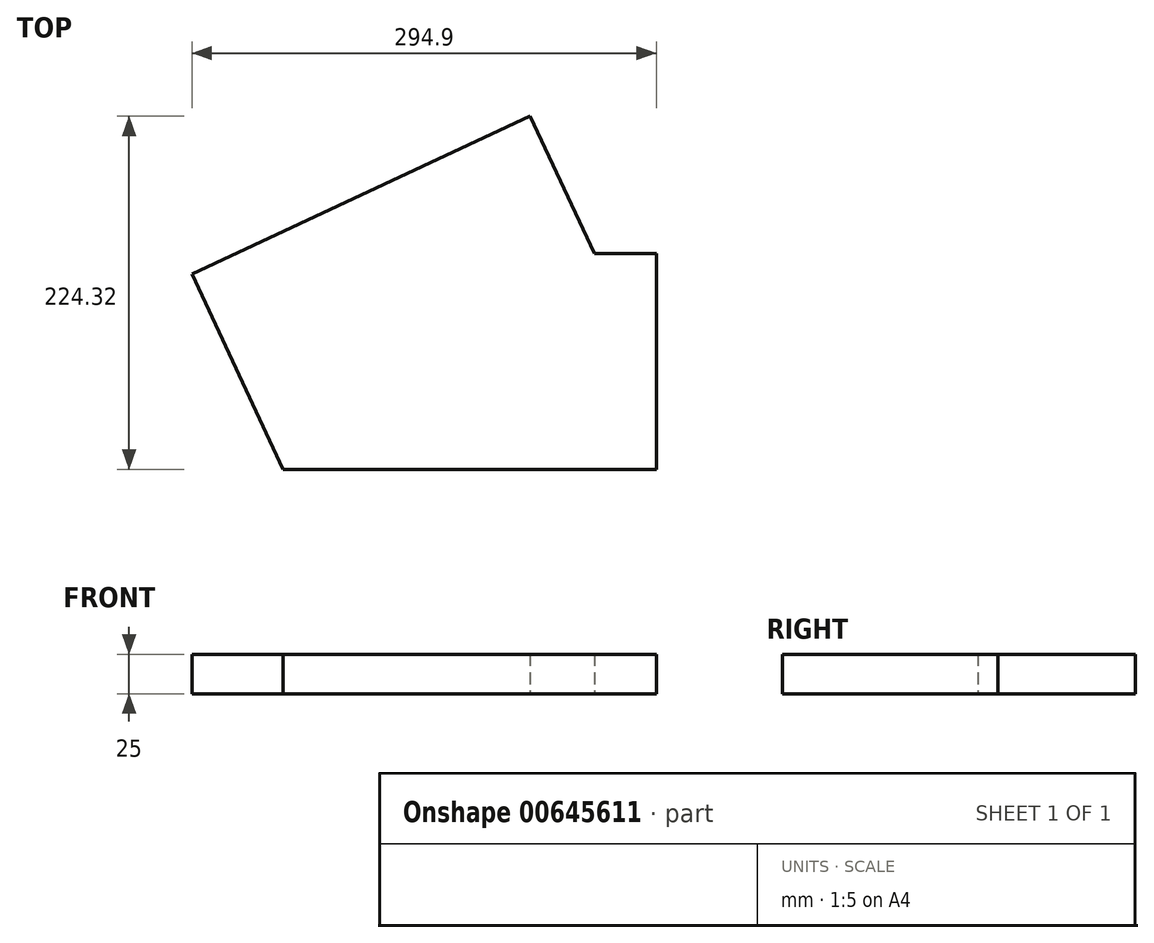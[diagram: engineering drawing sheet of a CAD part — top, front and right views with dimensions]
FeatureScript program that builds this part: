
annotation { "Feature Type Name" : "Feature", "Feature Type Description" : "" }
export const myFeature = defineFeature(function(context is Context, id is Id, definition is map)
    precondition{}
    {
        {
            var Q0;
            Q0=qCreatedBy(makeId("Top.planeOp"),FACE);
            var sketch = newSketch(context, id + "F0", { "sketchPlane" : qUnion([Q0])});
            skLineSegment(sketch, "E0.bottom", {"start": v(0, 137) * mm, "end": v(237, 137) * mm});
            skLineSegment(sketch, "E0.top", {"start": v(0, 0) * mm, "end": v(237, 0) * mm});
            skLineSegment(sketch, "E0.left", {"start": v(0, 137) * mm, "end": v(0, 0) * mm});
            skLineSegment(sketch, "E0.right", {"start": v(237, 137) * mm, "end": v(237, 0) * mm});
            skLineSegment(sketch, "E1.bottom", {"start": v(-57.9, 124.16) * mm, "end": v(156.9, 224.32) * mm});
            skLineSegment(sketch, "E1.top", {"start": v(0, 0) * mm, "end": v(214.8, 100.16) * mm});
            skLineSegment(sketch, "E1.left", {"start": v(-57.9, 124.16) * mm, "end": v(0, 0) * mm});
            skLineSegment(sketch, "E1.right", {"start": v(156.9, 224.32) * mm, "end": v(214.8, 100.16) * mm});
            skLineSegment(sketch, "E2", {"start": v(0, 0) * mm, "end": v(47.13, 21.98) * mm});
            skSolve(sketch);
        }
        {
            var Q0;
            Q0 = qSketchRegion(id + "F0", true);
            extrude(context, id + "F1", {"entities" : qUnion([Q0]), "depth" : 25 * mm, "offsetDistance" : 25 * mm});
        }
    });
